# Revit family: QF_BOURGEAT_Satellite4G_froid_1-1_entree530_vitree_ouverture_gauche
name_source: partatom
category: Equipement spécialisé
revit_build: Autodesk Revit 2015 (Build: 20140606_1530(x64)
units: mm (PartAtom-declared; Revit-internal decimal feet)

## types (3) — shared parameters
Certification = NF hygiene alimentaire
Classe Climatique = 4
Diametre_roue = 160 mm  [stored 0.524934 ft]
Fabricant = BOURGEAT
Fréquence = 50 Hz
Hauteur_poignee_porte_sol = 426 mm  [stored 1.39764 ft]
Hauteur_roue = 200 mm  [stored 0.656168 ft]
Indice de protection = IP25
Largeur_porte = 706 mm  [stored 2.31627 ft]
Longueur hors tout = 791 mm
Longueur_poignees_laterales = 648 mm  [stored 2.12598 ft]
Materiau_Poignee_porte = B_Elastomère_TPE_S
Materiau_bac = B_Elastomère_TPE_S
Materiau_bandage = B_Elastomère_TPE_S
Materiau_porte = Acier inoxydable, brossé
Materiau_vitre = Verre, vitrage transparent, trempé
Materiaux_reserve_eau = Acrylique, transparent
Nature isolant = Mousse sans PU
Phase = 2
Poignee_gauche = Oui
Pos_IHM_bord_gauche_porte_gauche = 175 mm  [stored 0.574147 ft]
Pos_V_IHM = 98 mm  [stored 0.321522 ft]
Pos_vitre_bord_gauche_porte_gauche = 350 mm  [stored 1.14829 ft]
Profondeur hors tout = 804 mm  [stored 2.6378 ft]
Spécification du Fabricant = Satellite 4G
Tension = 230 V
Type Fluide Frigorigène = R134a
URL catalogue = http://www.bourgeat.fr

## per-type parameters (varying)
| type | Charge max | Charge_gaz | Consommation énergétique | Hauteur hors tout | Hauteur_poignees_laterales | Hauteur_porte | Intensite | Modèle | Poids net à vide | Puissance frigorifique | Puissance électrique  |
| GN10_sans_humidification_tirant_gauche | 100.00 kg | 0.150 Kg | 3 Kwh/h NFD40-016 | 1123 mm  [stored 3.68438 ft] | 804 mm  [stored 2.6378 ft] | 876 mm  [stored 2.87402 ft] | 1 A | 842110 | 100.00 kg | 270 W à-5°C | 300 W |
| GN15_sans_humidification_tirant_gauche | 150.00 kg | 0.150 Kg | 3.4 Kwh/h NFD40-016 | 1478 mm  [stored 4.84908 ft] | 937 mm  [stored 3.07415 ft] | 1231 mm  [stored 4.03871 ft] | 1 A | 842115 | 120.00 kg | 270 W à -5°C | 300 W |
| GN20_sans_humidification_tirant_gauche | 200.00 kg | 0.220 Kg | 3.8 Kwh/h NFD40-016 | 1833 mm  [stored 6.01378 ft] | 937 mm  [stored 3.07415 ft] | 1586 mm  [stored 5.20341 ft] | 2 A | 842121 | 140.00 kg | 465 W à -5°C | 500 W |

note: [stored X ft] marks values corroborated as IEEE doubles in the binary element streams (Revit-internal decimal feet)
